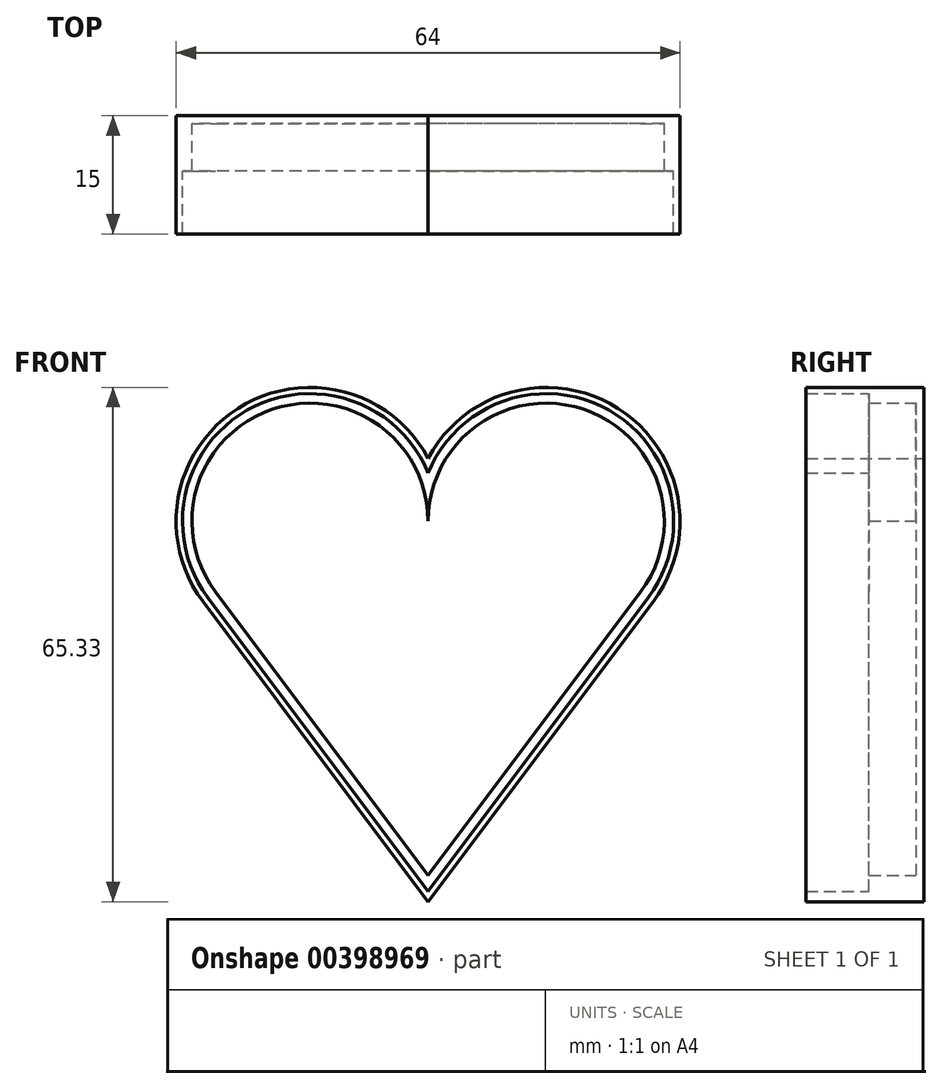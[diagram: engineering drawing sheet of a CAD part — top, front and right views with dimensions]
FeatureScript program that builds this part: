
annotation { "Feature Type Name" : "Feature", "Feature Type Description" : "" }
export const myFeature = defineFeature(function(context is Context, id is Id, definition is map)
    precondition{}
    {
        {
            var Q0;
            Q0=qCreatedBy(makeId("Front.planeOp"),FACE);
            var sketch = newSketch(context, id + "F0", { "sketchPlane" : qUnion([Q0])});
            skArc(sketch, "E0", {"start": v(0, 0) * mm, "mid": v(-19.74, 14.23) * mm, "end": v(-27, -9) * mm});
            skArc(sketch, "E1", {"start": v(27, -9) * mm, "mid": v(19.74, 14.23) * mm, "end": v(0, 0) * mm});
            skLineSegment(sketch, "E2", {"start": v(0, -45) * mm, "end": v(27, -9) * mm});
            skLineSegment(sketch, "E3", {"start": v(0, -45) * mm, "end": v(-27, -9) * mm});
            skPoint(sketch, "E4.start.orphan", {"position": v(0, 0) * mm});
            skArc(sketch, "E5.0", {"start": v(27.96, -9.72) * mm, "mid": v(22.98, 14.1) * mm, "end": v(0, 6.12) * mm});
            skLineSegment(sketch, "E5.1", {"start": v(0, -47) * mm, "end": v(27.96, -9.72) * mm});
            skLineSegment(sketch, "E5.2", {"start": v(0, -47) * mm, "end": v(-27.96, -9.72) * mm});
            skArc(sketch, "E5.3", {"start": v(0, 6.12) * mm, "mid": v(-22.98, 14.1) * mm, "end": v(-27.96, -9.72) * mm});
            skArc(sketch, "E6.0", {"start": v(0, 8) * mm, "mid": v(-24.13, 14.34) * mm, "end": v(-28.6, -10.2) * mm});
            skArc(sketch, "E6.1", {"start": v(28.6, -10.2) * mm, "mid": v(24.13, 14.34) * mm, "end": v(0, 8) * mm});
            skLineSegment(sketch, "E6.2", {"start": v(0, -48.33) * mm, "end": v(28.6, -10.2) * mm});
            skLineSegment(sketch, "E6.3", {"start": v(0, -48.33) * mm, "end": v(-28.6, -10.2) * mm});
            skSolve(sketch);
        }
        {
            var Q0;
            Q0=makeQuery(id+"F0.imprint","IMPRINT",FACE,{"disambiguationData":[TD([[makeQuery(id+"F0.imprint","IMPRINT",EDGE,{"derivedFrom":sQuery(id+"F0.wireOp",EDGE,"E5.0")}),-1.0]])]});
            var Q1;
            Q1=makeQuery(id+"F0.imprint","IMPRINT",FACE,{"disambiguationData":[TD([[makeQuery(id+"F0.imprint","IMPRINT",EDGE,{"derivedFrom":sQuery(id+"F0.wireOp",EDGE,"E0")}),1.0]])]});
            var Q2;
            Q2=makeQuery(id+"F0.imprint","IMPRINT",FACE,{"disambiguationData":[TD([[makeQuery(id+"F0.imprint","IMPRINT",EDGE,{"derivedFrom":sQuery(id+"F0.wireOp",EDGE,"E0")}),-1.0]])]});
            extrude(context, id + "F1", {"entities" : qUnion([Q0, Q1, Q2]), "depth" : 1 * mm});
        }
        {
            var Q0;
            Q0=makeQuery(id+"F0.imprint","IMPRINT",FACE,{"disambiguationData":[TD([[makeQuery(id+"F0.imprint","IMPRINT",EDGE,{"derivedFrom":sQuery(id+"F0.wireOp",EDGE,"E5.0")}),-1.0]])]});
            extrude(context, id + "F2", {"entities" : qUnion([Q0]), "operationType" : NewBodyOperationType.ADD, "depth" : 15 * mm});
        }
        {
            var Q0;
            Q0=makeQuery(id+"F0.imprint","IMPRINT",FACE,{"disambiguationData":[TD([[makeQuery(id+"F0.imprint","IMPRINT",EDGE,{"derivedFrom":sQuery(id+"F0.wireOp",EDGE,"E0")}),-1.0]])]});
            extrude(context, id + "F3", {"entities" : qUnion([Q0]), "operationType" : NewBodyOperationType.ADD, "depth" : 7 * mm});
        }
    });
